# Revit family: Grab_Bar-Bradley_Corp-Elvari_42L_Hooks_NoHooks
name_source: partatom
category: Specialty Equipment
units: mm (PartAtom-declared; Revit-internal decimal feet)

## family parameters
Always vertical = No
Cut with Voids When Loaded = No
Enable Cutting in Views = No
Maintain Annotation Orientation = No
Part Type = Normal
Room Calculation Point = No
Round Connector Dimension = Use Diameter
Shared = No
Work Plane-Based = No

## types (2) — shared parameters
Default Elevation = 0' - 0"
Design Status = 1
Manufacturer = Bradley Corporation
Manufacturer Installation URL - English = https://www.bradleycorp.com
Product Page URL = https://www.bradleycorp.com
Product Tech Data URL - English = https://www.bradleycorp.com
Specifications URL = https://www.bradleycorp.com

## per-type parameters (varying)
| type | Description | Hooks |
| 8B1-0014296 - Hooks | 42" Grab Bar with Hooks | Yes |
| 8B1-0014200 - No Hooks | 42" Grab Bar No Hooks | No |

note: column(s) folded — value = type name in every type: Model

## geometry (parser evidence)
native form markers: Blend x4, Sweep x16
no freeform markers — native parametric forms only
